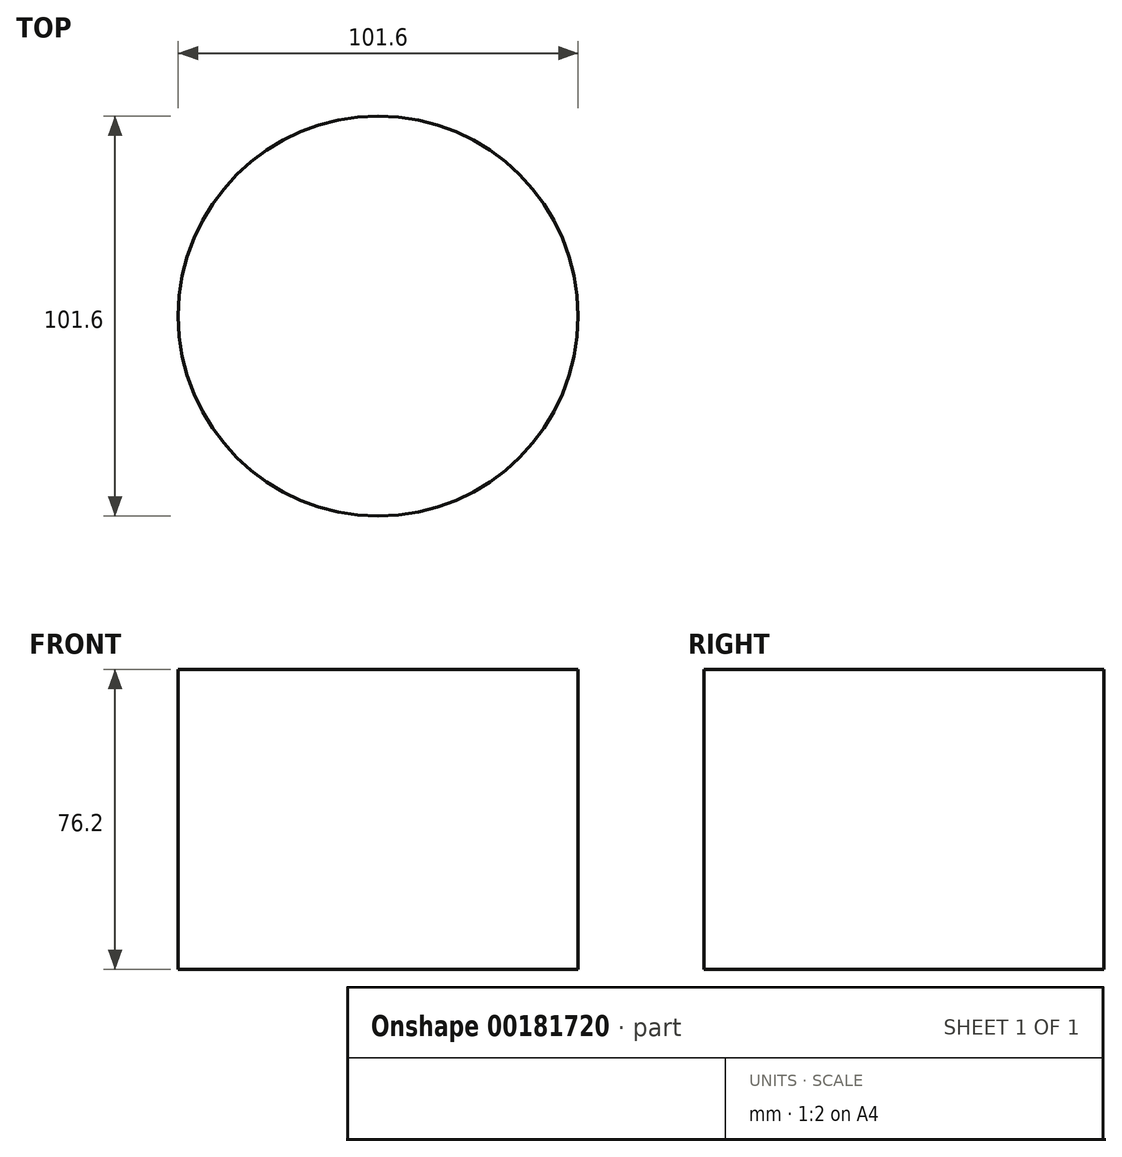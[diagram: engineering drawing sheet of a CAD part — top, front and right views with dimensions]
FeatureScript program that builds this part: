
annotation { "Feature Type Name" : "Feature", "Feature Type Description" : "" }
export const myFeature = defineFeature(function(context is Context, id is Id, definition is map)
    precondition{}
    {
        {
            var Q0;
            Q0=qCreatedBy(makeId("Top.planeOp"),FACE);
            var sketch = newSketch(context, id + "F0", { "sketchPlane" : qUnion([Q0])});
            skCircle(sketch, "E0", {"center": v(0, 0) * mm, "radius": 50.8 * mm});
            skSolve(sketch);
        }
        {
            var Q0;
            Q0 = qSketchRegion(id + "F0", true);
            extrude(context, id + "F1", {"entities" : qUnion([Q0]), "depth" : 76.2 * mm});
        }
    });
